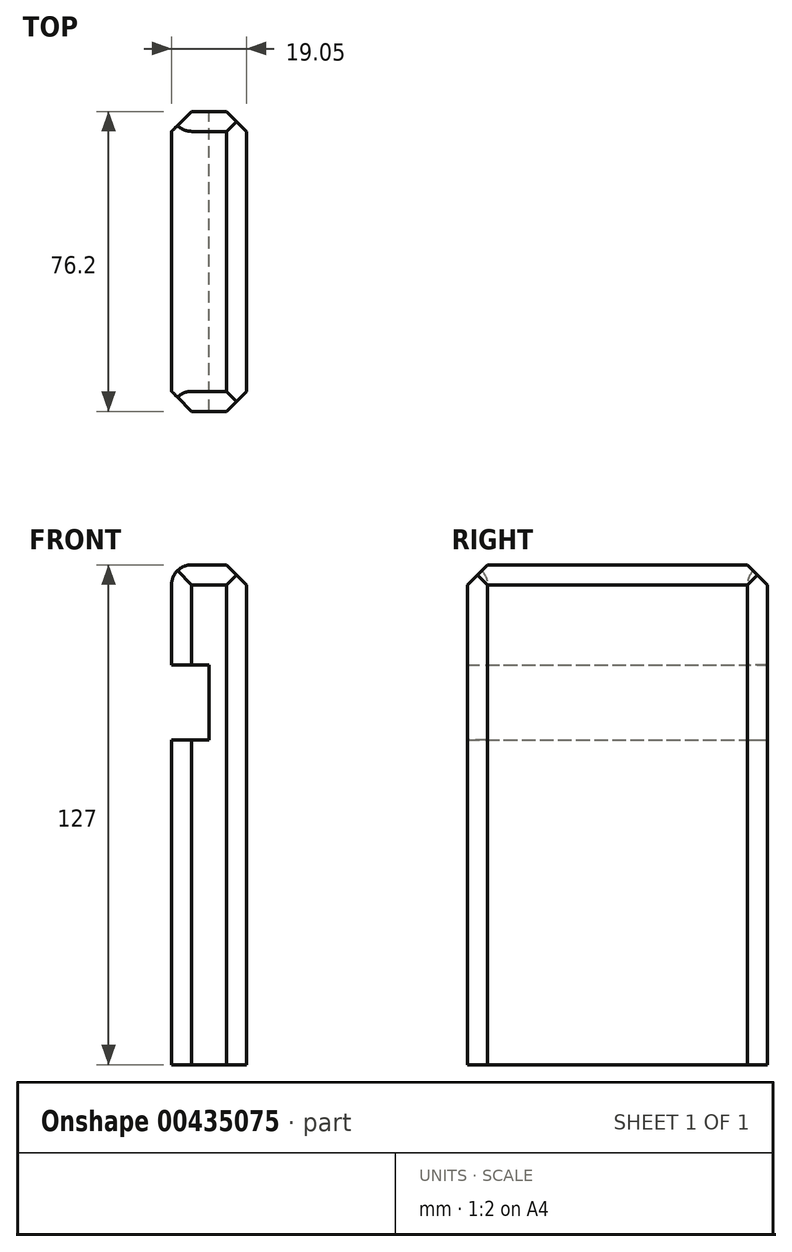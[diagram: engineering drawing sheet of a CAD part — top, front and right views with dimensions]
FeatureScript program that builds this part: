
annotation { "Feature Type Name" : "Feature", "Feature Type Description" : "" }
export const myFeature = defineFeature(function(context is Context, id is Id, definition is map)
    precondition{}
    {
        {
            var Q0;
            Q0=qCreatedBy(makeId("Front.planeOp"),FACE);
            var sketch = newSketch(context, id + "F0", { "sketchPlane" : qUnion([Q0])});
            skLineSegment(sketch, "E0", {"start": v(29.77, 109.1) * mm, "end": v(10.72, 109.1) * mm});
            skLineSegment(sketch, "E1", {"start": v(10.72, 109.1) * mm, "end": v(10.72, 83.7) * mm});
            skLineSegment(sketch, "E2", {"start": v(10.72, 83.7) * mm, "end": v(20.25, 83.7) * mm});
            skLineSegment(sketch, "E3", {"start": v(20.25, 83.7) * mm, "end": v(20.25, 64.65) * mm});
            skLineSegment(sketch, "E4", {"start": v(20.25, 64.65) * mm, "end": v(10.72, 64.65) * mm});
            skLineSegment(sketch, "E5", {"start": v(10.72, 64.65) * mm, "end": v(10.72, -17.9) * mm});
            skLineSegment(sketch, "E6", {"start": v(10.72, -17.9) * mm, "end": v(29.77, -17.9) * mm});
            skLineSegment(sketch, "E7", {"start": v(29.77, -17.9) * mm, "end": v(29.77, 109.1) * mm});
            skSolve(sketch);
        }
        {
            var Q0;
            Q0 = qSketchRegion(id + "F0", true);
            extrude(context, id + "F1", {"entities" : qUnion([Q0]), "depth" : 76.2 * mm});
        }
        {
            var Q0;
            Q0=makeQuery(id+"F1.opExtrude","SWEPT_EDGE",EDGE,{"disambiguationData":[OSD([sQuery(id+"F0.wireOp",EDGE,"E0"),sQuery(id+"F0.wireOp",EDGE,"E7")])]});
            chamfer(context, id + "F2", {"entities" : qUnion([Q0]), "width" : 5.08 * mm, "tangentPropagation" : true});
        }
        {
            var Q0;
            Q0=makeQuery(id+"F1.opExtrude","CAP_EDGE",EDGE,{"disambiguationData":[OSD([sQuery(id+"F0.wireOp",EDGE,"E0")])],"isStart":false});
            var Q1;
            Q1=makeQuery(id+"F1.opExtrude","CAP_EDGE",EDGE,{"disambiguationData":[OSD([sQuery(id+"F0.wireOp",EDGE,"E0")])],"isStart":true});
            chamfer(context, id + "F3", {"entities" : qUnion([Q0, Q1]), "width" : 5.08 * mm, "tangentPropagation" : true});
        }
        {
            var Q0;
            Q0=makeQuery(id+"F1.opExtrude","SWEPT_EDGE",EDGE,{"disambiguationData":[OSD([sQuery(id+"F0.wireOp",EDGE,"E0"),sQuery(id+"F0.wireOp",EDGE,"E1")])]});
            fillet(context, id + "F4", {"entities" : qUnion([Q0]), "radius" : 5.08 * mm, "tangentPropagation" : true, "allowEdgeOverflow" : false});
        }
        {
            var Q0;
            Q0=makeQuery(id+"F1.opExtrude","CAP_EDGE",EDGE,{"disambiguationData":[OSD([sQuery(id+"F0.wireOp",EDGE,"E1")])],"isStart":false});
            var Q1;
            Q1=makeQuery(id+"F1.opExtrude","CAP_EDGE",EDGE,{"disambiguationData":[OSD([sQuery(id+"F0.wireOp",EDGE,"E7")])],"isStart":false});
            var Q2;
            Q2=makeQuery(id+"F1.opExtrude","CAP_EDGE",EDGE,{"disambiguationData":[OSD([sQuery(id+"F0.wireOp",EDGE,"E5")])],"isStart":false});
            var Q3;
            Q3=makeQuery(id+"F1.opExtrude","CAP_EDGE",EDGE,{"disambiguationData":[OSD([sQuery(id+"F0.wireOp",EDGE,"E7")])],"isStart":true});
            var Q4;
            Q4=makeQuery(id+"F1.opExtrude","CAP_EDGE",EDGE,{"disambiguationData":[OSD([sQuery(id+"F0.wireOp",EDGE,"E1")])],"isStart":true});
            var Q5;
            Q5=makeQuery(id+"F1.opExtrude","CAP_EDGE",EDGE,{"disambiguationData":[OSD([sQuery(id+"F0.wireOp",EDGE,"E5")])],"isStart":true});
            chamfer(context, id + "F5", {"entities" : qUnion([Q0, Q1, Q2, Q3, Q4, Q5]), "width" : 5.08 * mm, "tangentPropagation" : true});
        }
    });
